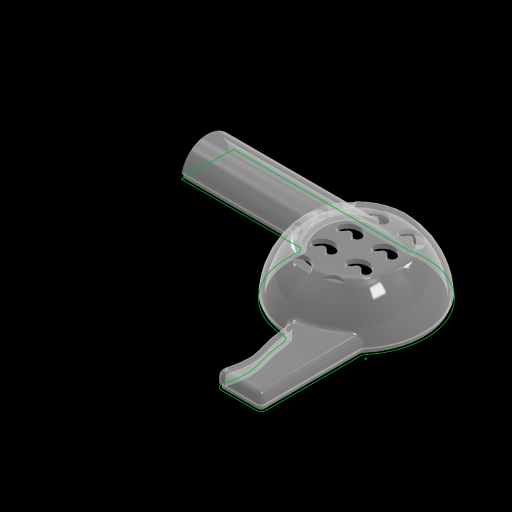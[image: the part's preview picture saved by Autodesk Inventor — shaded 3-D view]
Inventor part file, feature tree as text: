
AUTODESK INVENTOR PART (.ipt)
format: ipt  version: 2024 (Build 280153000, 153)  size: 648,704 bytes
history: native  units: in
note: dims shown in document units (in); Inventor stores cm internally (conversion verified against a paired STEP export)
features: sketch x10, plane x3, fillet x2, extrude x2, other x1, loft x1, shell x1, pattern_linear x1, sweep x1
ambient origin geometry x8: Origin, YZ Plane, XZ Plane, XY Plane, X Axis, Y Axis, Z Axis, Center Point
bodies: Solid1 (feature_tree)
feature tree (22):
  other  "BOWL SHAPE"
  fillet  "Fillet1"  Radius=4.0in
  plane  "Work Plane HANDLE1"
  plane  "Work Plane2 HANDLE2"
  plane  "Work Plane HANDLE 3"
  loft  "Loft1"
  extrude  "Extrusion1"  Depth=2.5in
  fillet  "Fillet2"  Radius=1.5in
  shell  "Shell1"  Thickness=0.5in
  extrude  "SINGLE VENT HOLE"  Depth=1.4in
  pattern_linear  "VENT PATTERN"  Spacing1=0.5in  [1 undecoded]
  sketch  "Sketch10"  dims[d16=0.25in]
  sweep  "Sweep2"
  sketch  "Sketch1"  dims[d2=1.5in d3=90.0deg]
  sketch  "Sketch2"  dims[d4=0.25in d5=2.5in d6=3.5in d7=4.25in d8=1.5in d9=0.5in]
  sketch  "Sketch3"  dims[d10=0.25in d11=1.4in]
  sketch  "Sketch4"  dims[d12=0.5in]
  sketch  "Sketch5"  dims[d13=0.25in]
  sketch  "Sketch6"  dims[d14=1.2in]
  sketch  "Sketch7"  dims[d15=0.5in]
  sketch  "Sketch11"  dims[d18=1.35in d19=0.5in d20=0.25in d21=0.0in d22=90.0deg d23=0.0in d24=90.0deg d25=0.0in d26=90.0deg d27=0.0in d28=90.0deg d29=0.75in d30=1.2in d31=5.5in d32=0.0in d33=0.15in d34=0.125in d35=0.125in d36=0.0in d37=4.3307in d39=1.0in d40=4.3307in d42=0.75in d45=0.1206in d46=0.3445in d50=3.4745in d51=3.0631in d56=0.125in d57=0.0625in d58=0.0in d59=0.0in]
  sketch  "3D Sketch1"
note: 1 required parameter value undecoded (feature->parameter linkage not recoverable at this tier; creation-order binding heuristic only, values carry confidence <= 0.55)
